# Revit family: BE_84542_de_DE
name_source: partatom
category: Leuchten
revit_build: Autodesk Revit 2015 (Build: 20160512_0715(x64)
units: mm (PartAtom-declared; Revit-internal decimal feet)

## types (3) — shared parameters
AC/DC = AC/DC
Aktualisierung = 2017-07-27T04:09:25
BEGA_Dummy = Nein
BEGA_Intern = Ja
BEGA_Intern_Konstruktion = Ja
BEGA_Intern_an = Ja
BEGA_Intern_aus = Ja
Beschreibung = Hochleistungsscheinwerfer
Beschreibung_Sonderanfertigung = Hier können Sie Informationen zur Sonderanfertigung eintragen.
CE_Konformität = ja
Energieeffizienzklasse = LED A++ - A
Farbwiedergabeindex = Ra > 80
Frequenz = 0/50-60 Hz
Hersteller = BEGA
Lampe = LED 303 W
Lastklassifizierung = Beleuchtung
Lebensdauerkriterien = L70B50 @ 25 °C =  h
Logo = BEGA_Logo.png
M_A = Nein
M_G = Ja
M_W = Nein
Material_02 = BEGA_Oberfläche_Silber_matt
Material_03 = BEGA_Oberfläche_Weiss_matt
Material_04 = BEGA_Kunststoff_Grafit_matt
Material_06 = BEGA_Oberfläche_Edelstahl_gebürstet
Material_09 = BEGA_Glas_klar
Material_11 = BEGA_Glas_opal
Material_12 = BEGA_Kunststoff_klar
Material_15 = BEGA_Leuchtmedium_matt
Material_17 = BEGA_Reflektor
Material_18 = BEGA_Gummi_schwarz
Produktdatenblatt = http://www.bega.de
Scheinlast = 0 VA
Schutzart = IP 67
Schutzklasse = I
Sonderanfertigung = Nein
Spannung = 240 V
Typenbild = 84542.png
URL = http://www.bega.de
Umgebungstemperatur = 25 °C
Windangriffsfläche = 0.2 m²
zero-valued in all types: Vorgabe-Ansicht

## per-type parameters (varying)
| type | BEGA_IES1 | BEGA_IES2 | BEGA_IES3 | Bestellnummer | Farbtemperatur | LED_Modulbezeichnung | Lampenlichtstrom | Leuchtenlichtstrom | Modell |
| BEGA_84542_Grafit_K2 | Nein | Nein | Ja | 84542K2 | 2700 K | 6x LED-0688/840 | 54420 lm | 41750 lm | 84542K2 |
| BEGA_84542_Grafit_K4 | Nein | Ja | Nein | 84542 | 4000 K | 6x LED-0688/840 | 54420 lm | 41750 lm | 84542 |
| BEGA_84542_Grafit_K3 | Ja | Nein | Nein | 84542K3 | 3000 K | 6x LED-0688/830 | 52800 lm | 40507 lm | 84542K3 |

## geometry (parser evidence)
native form markers: Blend x2, Sweep x16
no freeform markers — native parametric forms only
